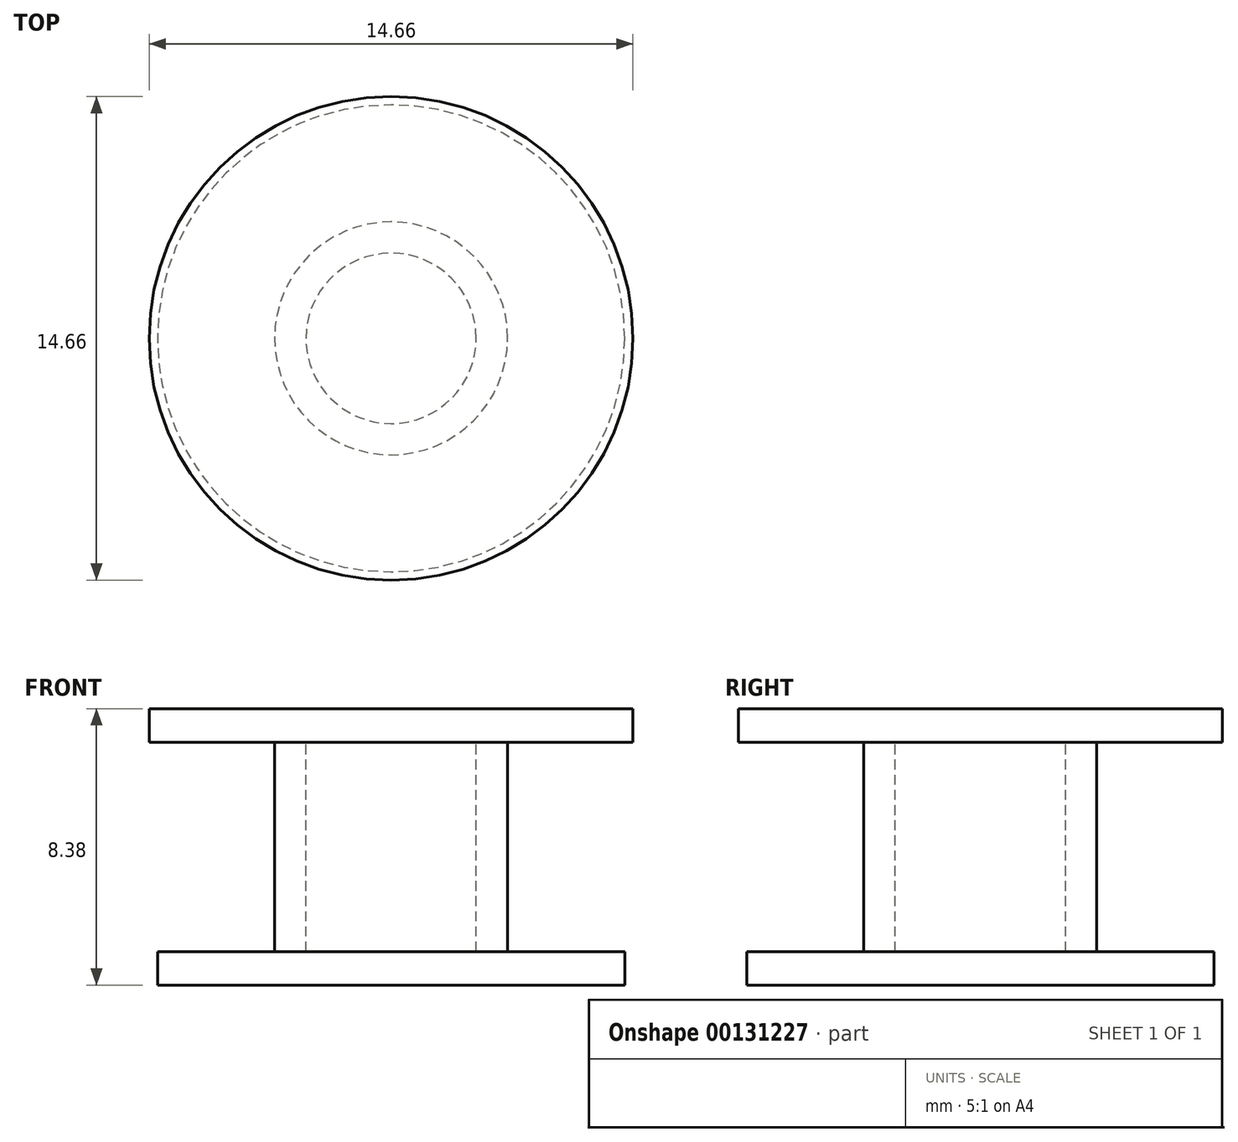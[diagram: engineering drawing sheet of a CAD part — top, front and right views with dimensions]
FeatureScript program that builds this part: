
annotation { "Feature Type Name" : "Feature", "Feature Type Description" : "" }
export const myFeature = defineFeature(function(context is Context, id is Id, definition is map)
    precondition{}
    {
        {
            var Q0;
            Q0=qCreatedBy(makeId("Top.planeOp"),FACE);
            var sketch = newSketch(context, id + "F0", { "sketchPlane" : qUnion([Q0])});
            skCircle(sketch, "E0", {"center": v(0, 0) * mm, "radius": 7.08 * mm});
            skSolve(sketch);
        }
        {
            var Q0;
            Q0=makeQuery(id+"F0.imprint","IMPRINT",FACE,{"disambiguationData":[TD([[makeQuery(id+"F0.imprint","IMPRINT",EDGE,{"derivedFrom":sQuery(id+"F0.wireOp",EDGE,"E0")}),1.0]])]});
            extrude(context, id + "F1", {"entities" : qUnion([Q0]), "depth" : 1.02 * mm});
        }
        {
            var Q0;
            Q0=makeQuery(id+"F1.opExtrude","CAP_FACE",FACE,{"disambiguationData":[OSD([sQuery(id+"F0.wireOp",EDGE,"E0")])],"isStart":false});
            var sketch = newSketch(context, id + "F2", { "sketchPlane" : qUnion([Q0])});
            skCircle(sketch, "E1", {"center": v(0, 0) * mm, "radius": 3.53 * mm});
            skSolve(sketch);
        }
        {
            var Q0;
            Q0 = qSketchRegion(id + "F2", true);
            extrude(context, id + "F3", {"entities" : qUnion([Q0]), "operationType" : NewBodyOperationType.ADD, "depth" : 6.35 * mm});
        }
        {
            var Q0;
            Q0=makeQuery(id+"F3.opExtrude","CAP_FACE",FACE,{"disambiguationData":[OSD([sQuery(id+"F2.wireOp",EDGE,"E1")])],"isStart":false});
            var sketch = newSketch(context, id + "F4", { "sketchPlane" : qUnion([Q0])});
            skCircle(sketch, "E2", {"center": v(0, 0) * mm, "radius": 2.58 * mm});
            skSolve(sketch);
        }
        {
            var Q0;
            Q0 = qSketchRegion(id + "F4", true);
            extrude(context, id + "F5", {"entities" : qUnion([Q0]), "operationType" : NewBodyOperationType.REMOVE, "oppositeDirection" : true, "depth" : 6.35 * mm});
        }
        {
            var Q0;
            Q0=makeQuery(id+"F3.opExtrude","CAP_FACE",FACE,{"disambiguationData":[OSD([sQuery(id+"F2.wireOp",EDGE,"E1")])],"isStart":false});
            var sketch = newSketch(context, id + "F6", { "sketchPlane" : qUnion([Q0])});
            skCircle(sketch, "E3", {"center": v(0, 0) * mm, "radius": 7.33 * mm});
            skSolve(sketch);
        }
        {
            var Q0;
            Q0 = qSketchRegion(id + "F6", true);
            extrude(context, id + "F7", {"entities" : qUnion([Q0]), "operationType" : NewBodyOperationType.ADD, "depth" : 1.02 * mm});
        }
    });
